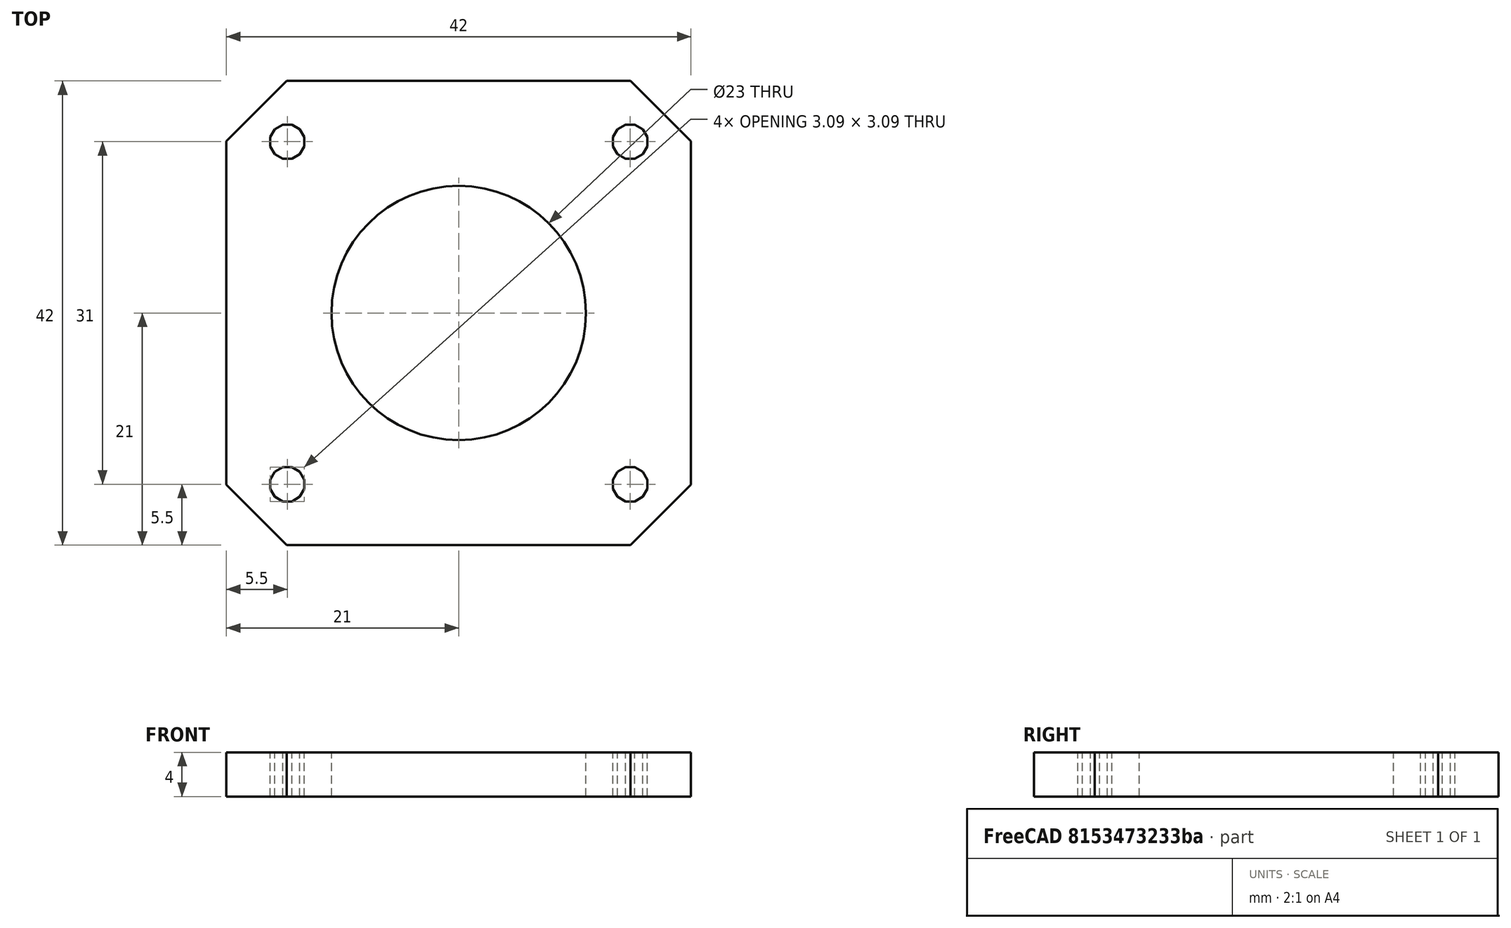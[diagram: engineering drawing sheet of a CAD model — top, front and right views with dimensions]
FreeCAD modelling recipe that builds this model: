
FCSTD DOCUMENT  (FreeCAD 0.14R3702 (Git))
Label: spacer
License: CC-BY 3.0
LicenseURL: http://creativecommons.org/licenses/by/3.0/
objects: Part::Box×5, Part::Fuse×5, Part::Prism×4, Part::MultiFuse×1, Part::Cylinder×1, Part::Cut×1
note: 17 computed .brp shape members not serialized (recipe doc carries the construction recipe); baked Part::Feature solids carry a one-line shape summary decoded from their .brp

FEATURE [Part::Box] cube
  Height = 4
  Length = 42
  Placement = pos=(-21,-21,0) rot=(0,0,1;0rad)
  Width = 42
FEATURE [Part::Box] cube001
  Height = 4.2
  Length = 5
  Placement = pos=(25.8345,-5,-0.1) rot=(0,0,1;0rad)
  Width = 10
FEATURE [Part::Prism] prism
  Circumradius = 1.6
  Height = 16
  Placement = pos=(21.9203,0,-8) rot=(0,0,1;0rad)
  Polygon = 12
FEATURE [Part::Fuse] union
  Base = -> cube001
  Placement = pos=(0,0,0) rot=(0,0,1;0.785398rad)
  Tool = -> prism
FEATURE [Part::Box] cube002
  Height = 4.2
  Length = 5
  Placement = pos=(25.8345,-5,-0.1) rot=(0,0,1;0rad)
  Width = 10
FEATURE [Part::Prism] prism001
  Circumradius = 1.6
  Height = 16
  Placement = pos=(21.9203,0,-8) rot=(0,0,1;0rad)
  Polygon = 12
FEATURE [Part::Fuse] union001
  Base = -> cube002
  Placement = pos=(0,0,0) rot=(0,0,1;2.35619rad)
  Tool = -> prism001
FEATURE [Part::Box] cube003
  Height = 4.2
  Length = 5
  Placement = pos=(25.8345,-5,-0.1) rot=(0,0,1;0rad)
  Width = 10
FEATURE [Part::Prism] prism002
  Circumradius = 1.6
  Height = 16
  Placement = pos=(21.9203,0,-8) rot=(0,0,1;0rad)
  Polygon = 12
FEATURE [Part::Fuse] union002
  Base = -> cube003
  Placement = pos=(0,0,0) rot=(0,0,1;3.92699rad)
  Tool = -> prism002
FEATURE [Part::Box] cube004
  Height = 4.2
  Length = 5
  Placement = pos=(25.8345,-5,-0.1) rot=(0,0,1;0rad)
  Width = 10
FEATURE [Part::Prism] prism003
  Circumradius = 1.6
  Height = 16
  Placement = pos=(21.9203,0,-8) rot=(0,0,1;0rad)
  Polygon = 12
FEATURE [Part::Fuse] union003
  Base = -> cube004
  Placement = pos=(0,0,0) rot=(0,0,-1;0.785398rad)
  Tool = -> prism003
FEATURE [Part::MultiFuse] Group
  Shapes = -> [union,union001,union002,union003]
FEATURE [Part::Cylinder] cylinder
  Angle = 360
  Height = 8.8
  Placement = pos=(0,0,-4.4) rot=(0,0,1;0rad)
  Radius = 11.5
FEATURE [Part::Fuse] union004
  Base = -> Group
  Tool = -> cylinder
FEATURE [Part::Cut] difference
  Base = -> cube
  Tool = -> union004
